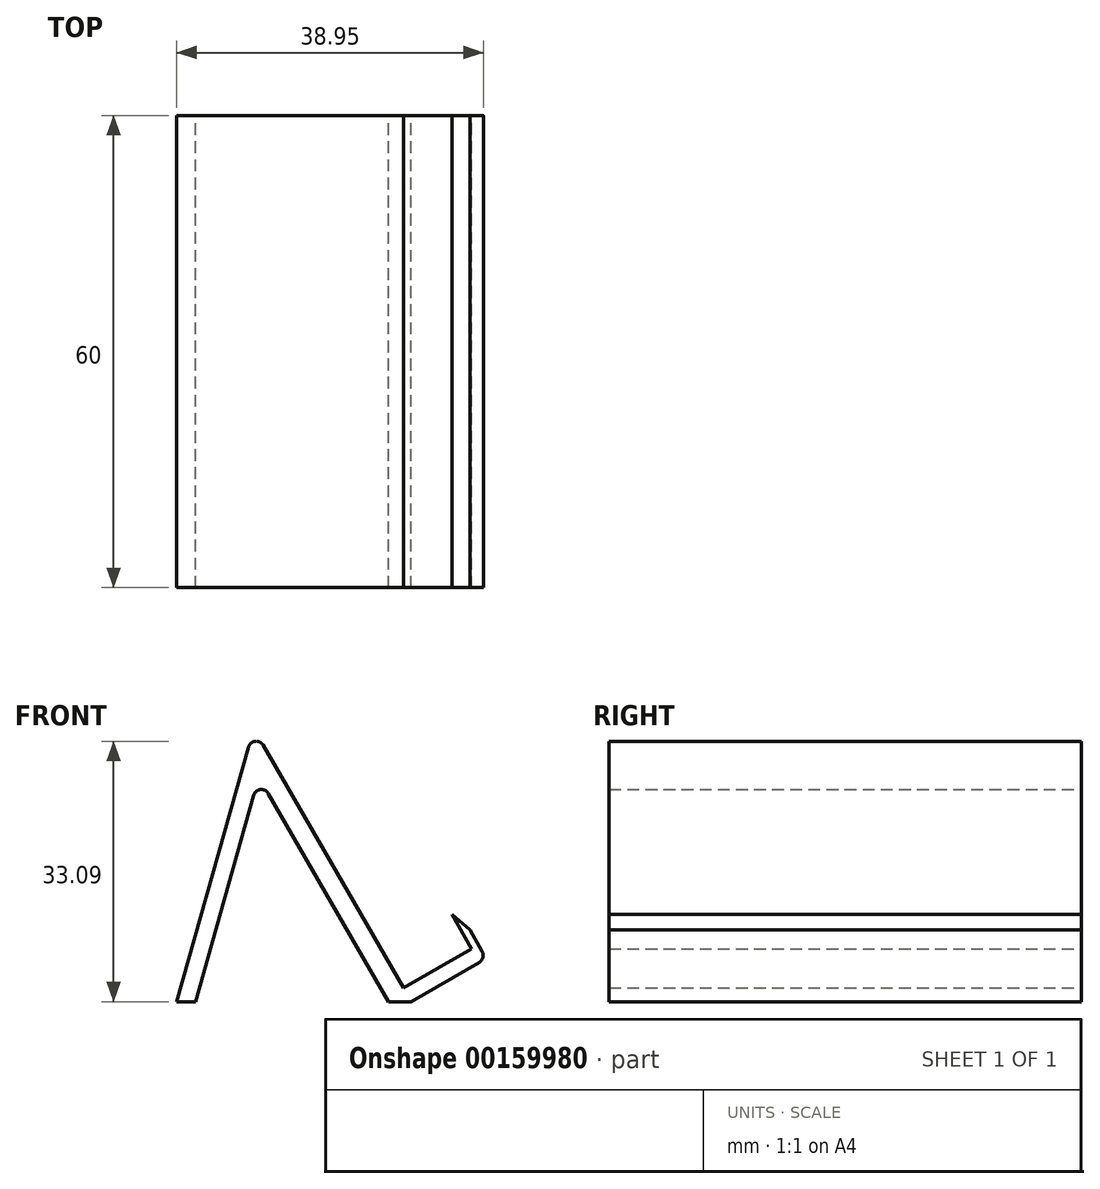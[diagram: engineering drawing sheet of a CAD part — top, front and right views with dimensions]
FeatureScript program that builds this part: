
annotation { "Feature Type Name" : "Feature", "Feature Type Description" : "" }
export const myFeature = defineFeature(function(context is Context, id is Id, definition is map)
    precondition{}
    {
        {
            var Q0;
            Q0=qCreatedBy(makeId("Front.planeOp"),FACE);
            var sketch = newSketch(context, id + "F0", { "sketchPlane" : qUnion([Q0])});
            skLineSegment(sketch, "E0", {"start": v(0, 0) * mm, "end": v(0, 34.64) * mm, "construction": true});
            skLineSegment(sketch, "E1", {"start": v(1.18, 32.59) * mm, "end": v(20, 0) * mm});
            skLineSegment(sketch, "E2", {"start": v(-0.64, 32.36) * mm, "end": v(-9.8, 0) * mm});
            skLineSegment(sketch, "E3", {"start": v(20, 0) * mm, "end": v(28.66, 5) * mm});
            skLineSegment(sketch, "E4", {"start": v(27.45, 9.09) * mm, "end": v(25.16, 11.06) * mm});
            skLineSegment(sketch, "E5", {"start": v(25.16, 11.06) * mm, "end": v(27.66, 6.73) * mm});
            skLineSegment(sketch, "E6", {"start": v(27.66, 6.73) * mm, "end": v(19, 1.73) * mm});
            skLineSegment(sketch, "E7", {"start": v(29.03, 6.37) * mm, "end": v(27.45, 9.09) * mm});
            skLineSegment(sketch, "E8", {"start": v(-9.8, 0) * mm, "end": v(-7.4, 0) * mm});
            skLineSegment(sketch, "E9", {"start": v(-7.4, 0) * mm, "end": v(0.01, 26.23) * mm});
            skLineSegment(sketch, "E10", {"start": v(1.84, 26.45) * mm, "end": v(17.11, 0) * mm});
            skLineSegment(sketch, "E11", {"start": v(17.11, 0) * mm, "end": v(20, 0) * mm});
            skPoint(sketch, "E12.visualSharp", {"position": v(0, 34.64) * mm});
            skArc(sketch, "E12.filletArc", {"start": v(1.18, 32.59) * mm, "mid": v(0.2, 33.08) * mm, "end": v(-0.64, 32.36) * mm});
            skPoint(sketch, "E13.visualSharp", {"position": v(0.66, 28.5) * mm});
            skArc(sketch, "E13.filletArc", {"start": v(1.84, 26.45) * mm, "mid": v(0.85, 26.95) * mm, "end": v(0.01, 26.23) * mm});
            skPoint(sketch, "E14.visualSharp", {"position": v(29.53, 5.5) * mm});
            skArc(sketch, "E14.filletArc", {"start": v(28.66, 5) * mm, "mid": v(29.13, 5.6) * mm, "end": v(29.03, 6.37) * mm});
            skSolve(sketch);
        }
        {
            var Q0;
            Q0 = qSketchRegion(id + "F0", true);
            extrude(context, id + "F1", {"entities" : qUnion([Q0]), "depth" : 60 * mm});
        }
    });
